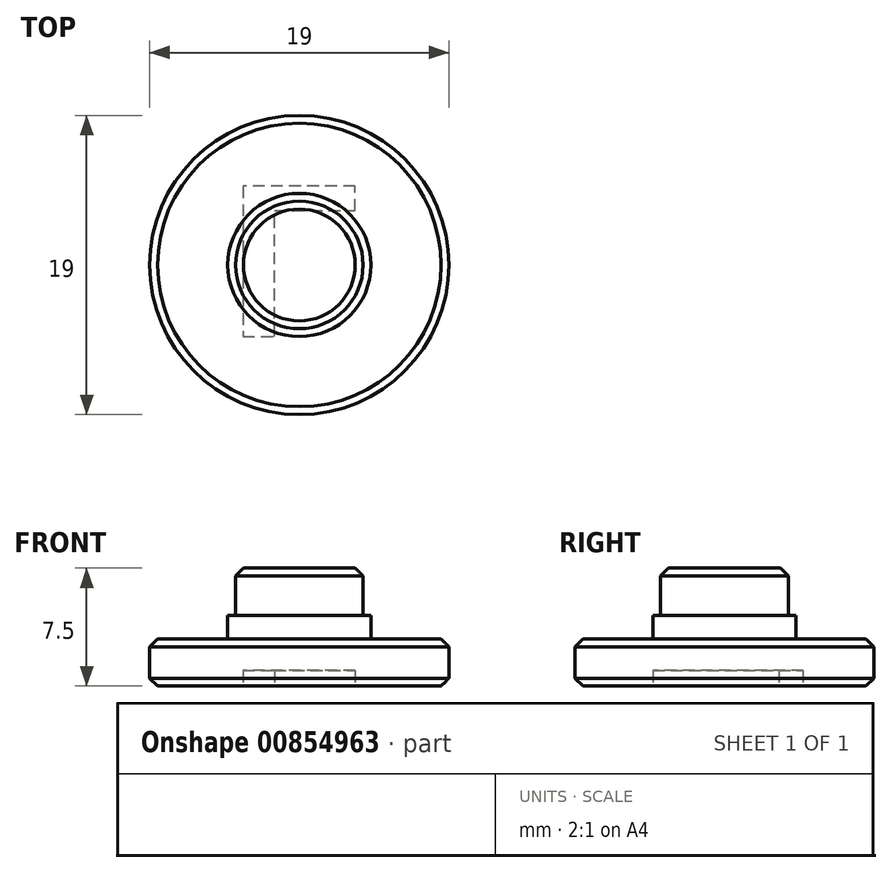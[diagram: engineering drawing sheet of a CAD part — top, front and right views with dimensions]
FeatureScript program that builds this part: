
annotation { "Feature Type Name" : "Feature", "Feature Type Description" : "" }
export const myFeature = defineFeature(function(context is Context, id is Id, definition is map)
    precondition{}
    {
        {
            var Q0;
            Q0=qCreatedBy(makeId("Top.planeOp"),FACE);
            var sketch = newSketch(context, id + "F0", { "sketchPlane" : qUnion([Q0])});
            skCircle(sketch, "E0", {"center": v(0, 0) * mm, "radius": 9.5 * mm});
            skSolve(sketch);
        }
        {
            var Q0;
            Q0=qSketchRegion(id+"F0",true);
            extrude(context, id + "F1", {"entities" : qUnion([Q0]), "depth" : 3 * mm, "offsetDistance" : 25 * mm});
        }
        {
            var Q0;
            Q0=makeQuery(id+"F1.opExtrude","CAP_FACE",FACE,{"disambiguationData":[OSD([sQuery(id+"F0.wireOp",EDGE,"E0")])],"isStart":false});
            var sketch = newSketch(context, id + "F2", { "sketchPlane" : qUnion([Q0])});
            skCircle(sketch, "E1", {"center": v(0, 0) * mm, "radius": 4.05 * mm});
            skSolve(sketch);
        }
        {
            var Q0;
            Q0=qSketchRegion(id+"F2",true);
            extrude(context, id + "F3", {"entities" : qUnion([Q0]), "operationType" : NewBodyOperationType.ADD, "depth" : 4.5 * mm, "offsetDistance" : 25 * mm});
        }
        {
            var Q0;
            Q0=makeQuery(id+"F3.opExtrude","CAP_EDGE",EDGE,{"disambiguationData":[OSD([sQuery(id+"F2.wireOp",EDGE,"E1")])],"isStart":false});
            var Q1;
            Q1=makeQuery(id+"F1.opExtrude","CAP_EDGE",EDGE,{"disambiguationData":[OSD([sQuery(id+"F0.wireOp",EDGE,"E0")])],"isStart":false});
            var Q2;
            Q2=makeQuery(id+"F1.opExtrude","CAP_EDGE",EDGE,{"disambiguationData":[OSD([sQuery(id+"F0.wireOp",EDGE,"E0")])],"isStart":true});
            chamfer(context, id + "F4", {"entities" : qUnion([Q0, Q1, Q2]), "width" : 0.5 * mm, "tangentPropagation" : true});
        }
        {
            var Q0;
            Q0=makeQuery(id+"F1.opExtrude","CAP_FACE",FACE,{"disambiguationData":[OSD([sQuery(id+"F0.wireOp",EDGE,"E0")])],"isStart":false});
            var sketch = newSketch(context, id + "F5", { "sketchPlane" : qUnion([Q0])});
            skCircle(sketch, "E2", {"center": v(0, 0) * mm, "radius": 4.55 * mm});
            skSolve(sketch);
        }
        {
            var Q0;
            Q0=qSketchRegion(id+"F5",true);
            extrude(context, id + "F6", {"entities" : qUnion([Q0]), "operationType" : NewBodyOperationType.ADD, "depth" : 1.5 * mm, "offsetDistance" : 25 * mm});
        }
        {
            var Q0;
            Q0=makeQuery(id+"F1.opExtrude","CAP_FACE",FACE,{"disambiguationData":[OSD([sQuery(id+"F0.wireOp",EDGE,"E0")])],"isStart":true});
            var sketch = newSketch(context, id + "F7", { "sketchPlane" : qUnion([Q0])});
            skText(sketch, "E3", { "text": "L", "fontName": "Arimo-Bold.ttf"});
            const initialGuessF7  = {"E3": [-0.00451, -0.005, 1, 0, 0.01]};
            skSetInitialGuess(sketch, initialGuessF7);
            skSolve(sketch);
        }
        {
            var Q0;
            Q0=qSketchRegion(id+"F7",true);
            extrude(context, id + "F8", {"entities" : qUnion([Q0]), "operationType" : NewBodyOperationType.REMOVE, "oppositeDirection" : true, "depth" : 1 * mm, "offsetDistance" : 25 * mm});
        }
    });
